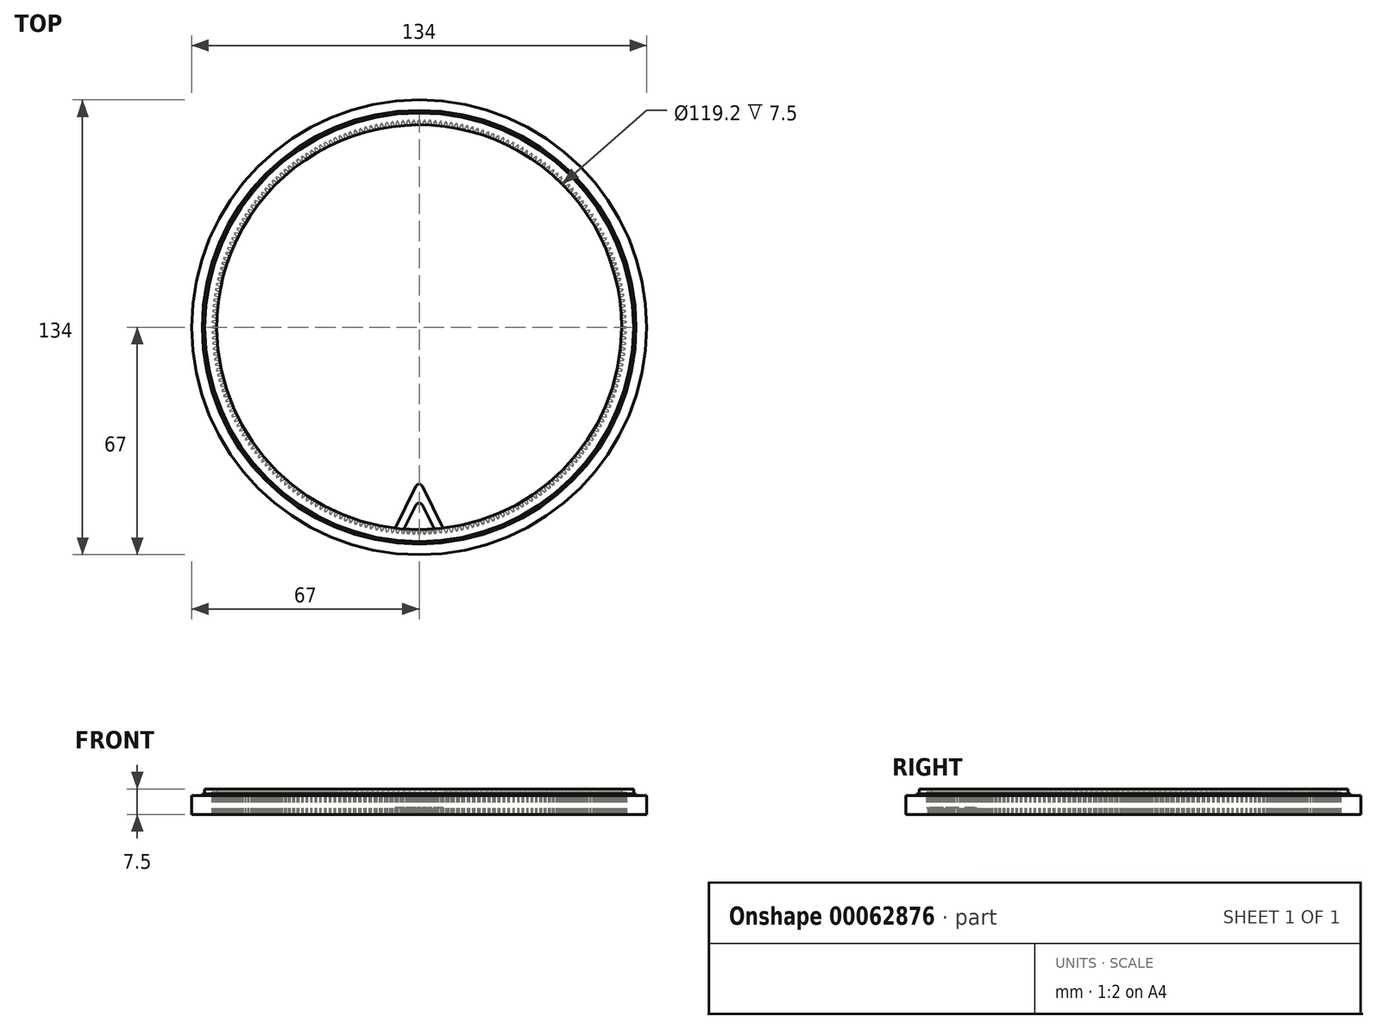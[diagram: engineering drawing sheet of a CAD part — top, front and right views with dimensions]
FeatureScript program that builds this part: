
annotation { "Feature Type Name" : "Feature", "Feature Type Description" : "" }
export const myFeature = defineFeature(function(context is Context, id is Id, definition is map)
    precondition{}
    {
        {
            var Q0;
            Q0=qCreatedBy(makeId("Top.planeOp"),FACE);
            var sketch = newSketch(context, id + "F0", { "sketchPlane" : qUnion([Q0])});
            skCircle(sketch, "E0", {"center": v(0, 0) * mm, "radius": 59.6 * mm});
            skCircle(sketch, "E1", {"center": v(0, 0) * mm, "radius": 67 * mm});
            skSolve(sketch);
        }
        {
            var Q0;
            Q0 = qSketchRegion(id + "F0", true);
            extrude(context, id + "F1", {"entities" : qUnion([Q0]), "endBound" : BoundingType.SYMMETRIC, "depth" : 7.5 * mm});
        }
        {
            var Q0;
            Q0=makeQuery(id+"F1.opExtrude","CAP_FACE",FACE,{"disambiguationData":[OSD([sQuery(id+"F0.wireOp",EDGE,"E0"),sQuery(id+"F0.wireOp",EDGE,"E1")])],"isStart":false});
            var sketch = newSketch(context, id + "F2", { "sketchPlane" : qUnion([Q0])});
            skCircle(sketch, "E2", {"center": v(0, 0) * mm, "radius": 63.88 * mm});
            skCircle(sketch, "E3", {"center": v(0, 0) * mm, "radius": 63.12 * mm});
            skSolve(sketch);
        }
        {
            var Q0;
            Q0 = qSketchRegion(id + "F2", true);
            extrude(context, id + "F3", {"entities" : qUnion([Q0]), "operationType" : NewBodyOperationType.REMOVE, "oppositeDirection" : true, "depth" : 1.5 * mm});
        }
        {
            var Q0;
            {var subQ0=sQuery(id+"F0.wireOp",EDGE,"E1");Q0=makeQuery(id+"F3.boolean.opBoolean","SPLIT",FACE,{"disambiguationData":[TD([makeQuery(id+"F1.opExtrude","SWEPT_FACE",FACE,{"disambiguationData":[OSD([subQ0])]})])],"derivedFrom":makeQuery(id+"F1.opExtrude","CAP_FACE",FACE,{"disambiguationData":[OSD([sQuery(id+"F0.wireOp",EDGE,"E0"),subQ0])],"isStart":false})});}
            extrude(context, id + "F4", {"entities" : qUnion([Q0]), "operationType" : NewBodyOperationType.REMOVE, "oppositeDirection" : true, "depth" : 2 * mm});
        }
        {
            var Q0;
            Q0=makeQuery(id+"F1.opExtrude","CAP_FACE",FACE,{"disambiguationData":[OSD([sQuery(id+"F0.wireOp",EDGE,"E0"),sQuery(id+"F0.wireOp",EDGE,"E1")])],"isStart":true});
            var sketch = newSketch(context, id + "F5", { "sketchPlane" : qUnion([Q0])});
            skCircle(sketch, "E4", {"center": v(0, 0) * mm, "radius": 61 * mm, "construction": true});
            skLineSegment(sketch, "E5", {"start": v(0, 0) * mm, "end": v(61, 0) * mm, "construction": true});
            skLineSegment(sketch, "E6", {"start": v(61, 0.15) * mm, "end": v(61, -0.15) * mm});
            skPoint(sketch, "E7", {"position": v(59.4, 0) * mm});
            skLineSegment(sketch, "E8", {"start": v(59.4, 0.68) * mm, "end": v(59.4, -0.68) * mm});
            skLineSegment(sketch, "E9", {"start": v(59.4, 0.68) * mm, "end": v(61, 0.15) * mm});
            skLineSegment(sketch, "E10", {"start": v(59.4, -0.68) * mm, "end": v(61, -0.15) * mm});
            skSolve(sketch);
        }
        {
            var Q0;
            Q0 = qSketchRegion(id + "F5", true);
            extrude(context, id + "F6", {"entities" : qUnion([Q0]), "operationType" : NewBodyOperationType.REMOVE, "oppositeDirection" : true, "depth" : 6.5 * mm});
        }
        {
            var Q0;
            Q0=makeQuery(id+"F6.boolean.opBoolean","COPY",FACE,{"derivedFrom":makeQuery(id+"F6.opExtrude","SWEPT_FACE",FACE,{"disambiguationData":[OSD([sQuery(id+"F5.wireOp",EDGE,"E9")])]})});
            var Q1;
            Q1=makeQuery(id+"F6.boolean.opBoolean","COPY",FACE,{"derivedFrom":makeQuery(id+"F6.opExtrude","SWEPT_FACE",FACE,{"disambiguationData":[OSD([sQuery(id+"F5.wireOp",EDGE,"E6")])]})});
            var Q2;
            Q2=makeQuery(id+"F6.boolean.opBoolean","COPY",FACE,{"derivedFrom":makeQuery(id+"F6.opExtrude","SWEPT_FACE",FACE,{"disambiguationData":[OSD([sQuery(id+"F5.wireOp",EDGE,"E10")])]})});
            var Q3;
            Q3=makeQuery(id+"F6.boolean.opBoolean","COPY",FACE,{"derivedFrom":makeQuery(id+"F6.opExtrude","CAP_FACE",FACE,{"disambiguationData":[OSD([sQuery(id+"F5.wireOp",EDGE,"E6"),sQuery(id+"F5.wireOp",EDGE,"E8"),sQuery(id+"F5.wireOp",EDGE,"E9"),sQuery(id+"F5.wireOp",EDGE,"E10")])],"isStart":false})});
            var Q4;
            Q4=makeQuery(id+"F1.opExtrude","CAP_EDGE",EDGE,{"disambiguationData":[OSD([sQuery(id+"F0.wireOp",EDGE,"E1")])],"isStart":true});
            circularPattern(context, id + "F7", {"faces" : qUnion([Q0, Q1, Q2, Q3]), "axis" : qUnion([Q4]), "angle" : 360 * degree, "instanceCount" : 240, "equalSpace" : true, "patternType" : PatternType.FACE});
        }
        {
            var Q0;
            Q0=makeQuery(id+"F1.opExtrude","CAP_FACE",FACE,{"disambiguationData":[OSD([sQuery(id+"F0.wireOp",EDGE,"E0"),sQuery(id+"F0.wireOp",EDGE,"E1")])],"isStart":true});
            var sketch = newSketch(context, id + "F8", { "sketchPlane" : qUnion([Q0])});
            skCircle(sketch, "E11.0", {"center": v(0, 0) * mm, "radius": 63.12 * mm, "construction": true});
            skLineSegment(sketch, "E12", {"start": v(0, 0) * mm, "end": v(0, 45) * mm, "construction": true});
            skLineSegment(sketch, "E13", {"start": v(0, 0) * mm, "end": v(8.79, 62.51) * mm, "construction": true});
            skLineSegment(sketch, "E14", {"start": v(8.79, 62.51) * mm, "end": v(0, 62.51) * mm});
            skLineSegment(sketch, "E15", {"start": v(0, 45) * mm, "end": v(8.79, 62.51) * mm});
            skLineSegment(sketch, "E16.MirrorCS", {"start": v(-8.79, 62.51) * mm, "end": v(0, 62.51) * mm});
            skLineSegment(sketch, "E17.MirrorCS", {"start": v(0, 45) * mm, "end": v(-8.79, 62.51) * mm});
            skLineSegment(sketch, "E18.0", {"start": v(4.73, 60.01) * mm, "end": v(0, 60.01) * mm});
            skLineSegment(sketch, "E18.1", {"start": v(0, 50.57) * mm, "end": v(4.73, 60.01) * mm});
            skLineSegment(sketch, "E18.2", {"start": v(0, 50.57) * mm, "end": v(-4.73, 60.01) * mm});
            skLineSegment(sketch, "E18.3", {"start": v(-4.73, 60.01) * mm, "end": v(0, 60.01) * mm});
            skSolve(sketch);
        }
        {
            var Q0;
            Q0 = qSketchRegion(id + "F8", true);
            extrude(context, id + "F9", {"entities" : qUnion([Q0]), "operationType" : NewBodyOperationType.ADD, "oppositeDirection" : true, "depth" : 2 * mm});
        }
        {
            var Q0;
            Q0=makeQuery(id+"F9.opExtrude","SWEPT_EDGE",EDGE,{"disambiguationData":[OSD([sQuery(id+"F8.wireOp",EDGE,"E15"),sQuery(id+"F8.wireOp",EDGE,"E17.MirrorCS")])]});
            var Q1;
            Q1=makeQuery(id+"F9.opExtrude","SWEPT_EDGE",EDGE,{"disambiguationData":[OSD([sQuery(id+"F8.wireOp",EDGE,"E18.1"),sQuery(id+"F8.wireOp",EDGE,"E18.2")])]});
            fillet(context, id + "F10", {"entities" : qUnion([Q0, Q1]), "radius" : 1 * mm, "tangentPropagation" : true, "allowEdgeOverflow" : false});
        }
    });
